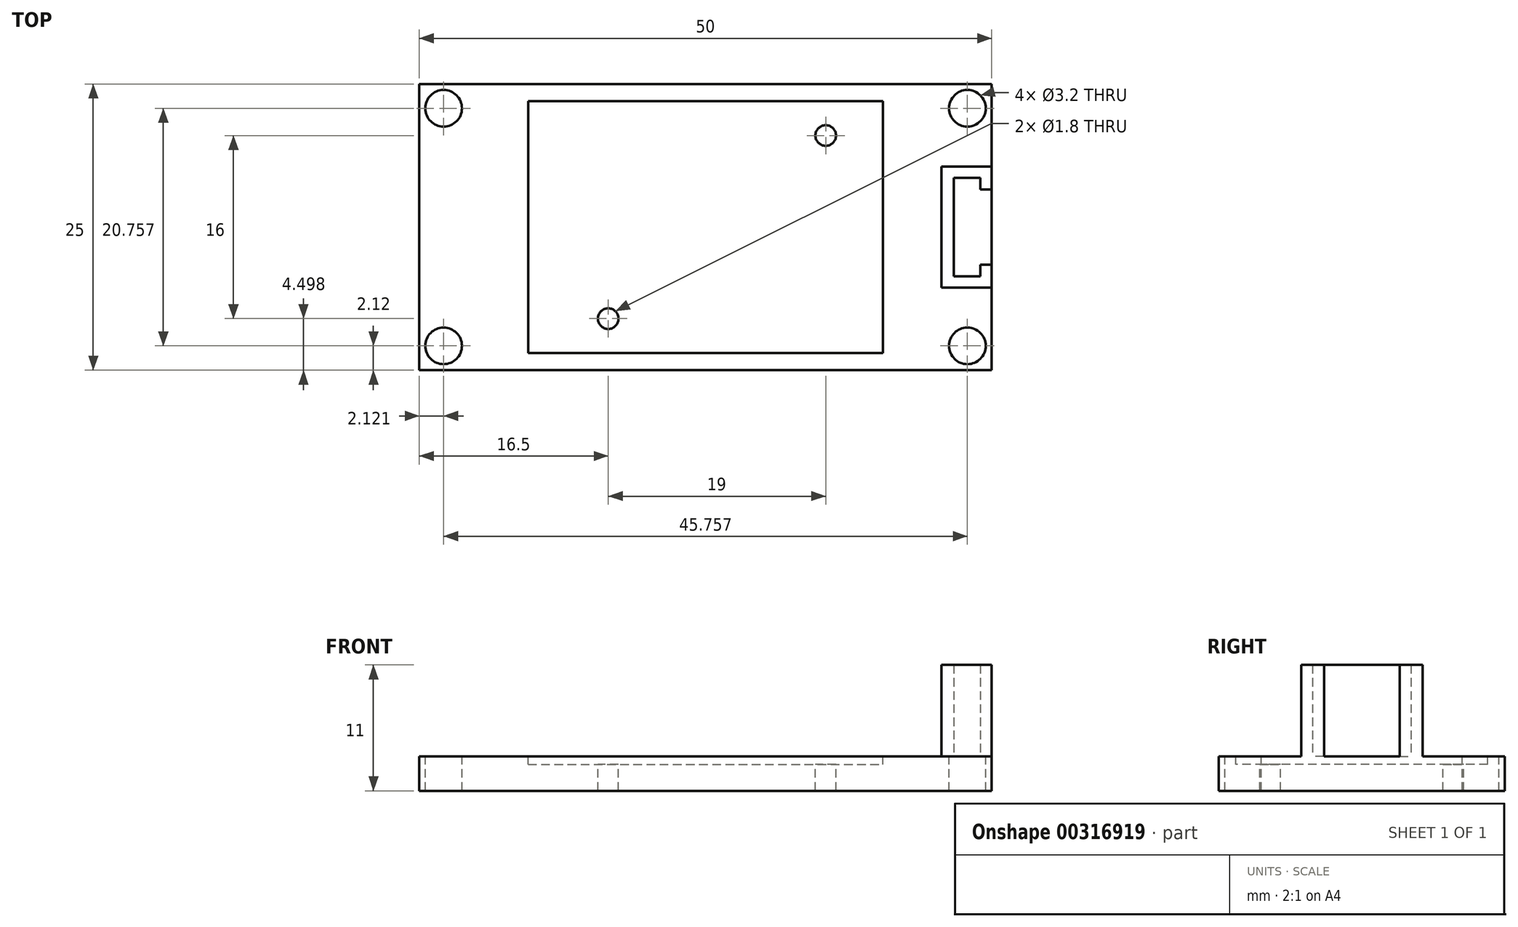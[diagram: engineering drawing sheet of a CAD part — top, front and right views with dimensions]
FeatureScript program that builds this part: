
annotation { "Feature Type Name" : "Feature", "Feature Type Description" : "" }
export const myFeature = defineFeature(function(context is Context, id is Id, definition is map)
    precondition{}
    {
        {
            var Q0;
            Q0=qCreatedBy(makeId("Top.planeOp"),FACE);
            var sketch = newSketch(context, id + "F0", { "sketchPlane" : qUnion([Q0])});
            skLineSegment(sketch, "E0.bottom", {"start": v(0, -1.45) * mm, "end": v(50, -1.45) * mm});
            skLineSegment(sketch, "E0.top", {"start": v(0, 23.55) * mm, "end": v(50, 23.55) * mm});
            skLineSegment(sketch, "E0.left", {"start": v(0, -1.45) * mm, "end": v(0, 23.55) * mm});
            skLineSegment(sketch, "E0.right", {"start": v(50, -1.45) * mm, "end": v(50, 23.55) * mm});
            skSolve(sketch);
        }
        {
            var Q0;
            Q0=makeQuery(id+"F0.imprint","IMPRINT",FACE,{"disambiguationData":[TD([[makeQuery(id+"F0.imprint","IMPRINT",EDGE,{"derivedFrom":sQuery(id+"F0.wireOp",EDGE,"E0.bottom")}),1.0]])]});
            extrude(context, id + "F1", {"entities" : qUnion([Q0]), "depth" : 3 * mm});
        }
        {
            var Q0;
            Q0=makeQuery(id+"F1.opExtrude","CAP_FACE",FACE,{"disambiguationData":[OSD([sQuery(id+"F0.wireOp",EDGE,"E0.bottom"),sQuery(id+"F0.wireOp",EDGE,"E0.top"),sQuery(id+"F0.wireOp",EDGE,"E0.left"),sQuery(id+"F0.wireOp",EDGE,"E0.right")])],"isStart":false});
            var sketch = newSketch(context, id + "F2", { "sketchPlane" : qUnion([Q0])});
            skLineSegment(sketch, "E1", {"start": v(0, 23.55) * mm, "end": v(2.12, 21.43) * mm});
            skLineSegment(sketch, "E2", {"start": v(50, 23.55) * mm, "end": v(47.88, 21.43) * mm});
            skLineSegment(sketch, "E3", {"start": v(50, -1.45) * mm, "end": v(47.88, 0.67) * mm});
            skLineSegment(sketch, "E4", {"start": v(0, -1.45) * mm, "end": v(2.12, 0.67) * mm});
            skSolve(sketch);
        }
        {
            var Q0;
            Q0=sQuery(id+"F2.wireOp",VERTEX,"E1.end");
            var Q1;
            Q1=sQuery(id+"F2.wireOp",VERTEX,"E2.end");
            var Q2;
            Q2=sQuery(id+"F2.wireOp",VERTEX,"E3.end");
            var Q3;
            Q3=sQuery(id+"F2.wireOp",VERTEX,"E4.end");
            var Q4;
            Q4=makeQuery(id+"F1.opExtrude","SWEPT_BODY",BODY,{"disambiguationData":[OSD([sQuery(id+"F0.wireOp",EDGE,"E0.bottom"),sQuery(id+"F0.wireOp",EDGE,"E0.top"),sQuery(id+"F0.wireOp",EDGE,"E0.left"),sQuery(id+"F0.wireOp",EDGE,"E0.right")])]});
            hole(context, id + "F3", {"style" : HoleStyle.SIMPLE, "endStyle" : HoleEndStyle.THROUGH, "holeDiameter" : 3.2 * mm, "isTappedThrough" : true, "tappedDepth" : 12 * mm, "tapClearance" : 3, "locations" : qUnion([Q0, Q1, Q2, Q3]), "scope" : qUnion([Q4])});
        }
        {
            var Q0;
            Q0=makeQuery(id+"F1.opExtrude","CAP_FACE",FACE,{"disambiguationData":[OSD([sQuery(id+"F0.wireOp",EDGE,"E0.bottom"),sQuery(id+"F0.wireOp",EDGE,"E0.top"),sQuery(id+"F0.wireOp",EDGE,"E0.left"),sQuery(id+"F0.wireOp",EDGE,"E0.right")])],"isStart":false});
            var sketch = newSketch(context, id + "F4", { "sketchPlane" : qUnion([Q0])});
            skLineSegment(sketch, "E5.bottom", {"start": v(9.5, 22.05) * mm, "end": v(40.5, 22.05) * mm});
            skLineSegment(sketch, "E5.top", {"start": v(9.5, 0.05) * mm, "end": v(40.5, 0.05) * mm});
            skLineSegment(sketch, "E5.left", {"start": v(9.5, 22.05) * mm, "end": v(9.5, 0.05) * mm});
            skLineSegment(sketch, "E5.right", {"start": v(40.5, 22.05) * mm, "end": v(40.5, 0.05) * mm});
            skSolve(sketch);
        }
        {
            var Q0;
            Q0=makeQuery(id+"F4.imprint","IMPRINT",FACE,{"disambiguationData":[TD([[makeQuery(id+"F4.imprint","IMPRINT",EDGE,{"derivedFrom":sQuery(id+"F4.wireOp",EDGE,"E5.bottom")}),-1.0]])]});
            extrude(context, id + "F5", {"entities" : qUnion([Q0]), "operationType" : NewBodyOperationType.REMOVE, "oppositeDirection" : true, "depth" : 0.7 * mm});
        }
        {
            var Q0;
            Q0=makeQuery(id+"F5.boolean.opBoolean","COPY",FACE,{"derivedFrom":makeQuery(id+"F5.opExtrude","CAP_FACE",FACE,{"disambiguationData":[OSD([sQuery(id+"F4.wireOp",EDGE,"E5.bottom"),sQuery(id+"F4.wireOp",EDGE,"E5.top"),sQuery(id+"F4.wireOp",EDGE,"E5.left"),sQuery(id+"F4.wireOp",EDGE,"E5.right")])],"isStart":false})});
            var sketch = newSketch(context, id + "F6", { "sketchPlane" : qUnion([Q0])});
            skLineSegment(sketch, "E6.bottom", {"start": v(10.5, 21.05) * mm, "end": v(39.5, 21.05) * mm});
            skLineSegment(sketch, "E6.top", {"start": v(10.5, 1.05) * mm, "end": v(39.5, 1.05) * mm});
            skLineSegment(sketch, "E6.left", {"start": v(10.5, 21.05) * mm, "end": v(10.5, 1.05) * mm});
            skLineSegment(sketch, "E6.right", {"start": v(39.5, 21.05) * mm, "end": v(39.5, 1.05) * mm});
            skPoint(sketch, "E7", {"position": v(10.5, 3.05) * mm});
            skPoint(sketch, "E8", {"position": v(16.5, 1.05) * mm});
            skPoint(sketch, "E9", {"position": v(35.5, 21.05) * mm});
            skPoint(sketch, "E10", {"position": v(39.5, 19.05) * mm});
            skLineSegment(sketch, "E11", {"start": v(35.5, 21.05) * mm, "end": v(35.5, 18.5) * mm});
            skLineSegment(sketch, "E12", {"start": v(39.5, 19.05) * mm, "end": v(34.03, 19.05) * mm});
            skLineSegment(sketch, "E13", {"start": v(10.5, 3.05) * mm, "end": v(17.92, 3.05) * mm});
            skLineSegment(sketch, "E14", {"start": v(16.5, 1.05) * mm, "end": v(16.5, 4.24) * mm});
            skPoint(sketch, "E15", {"position": v(35.5, 19.05) * mm});
            skPoint(sketch, "E16", {"position": v(16.5, 3.05) * mm});
            skSolve(sketch);
        }
        {
            var Q0;
            Q0=sQuery(id+"F6.wireOp",VERTEX,"E16");
            var Q1;
            Q1=sQuery(id+"F6.wireOp",VERTEX,"E15");
            var Q2;
            Q2=makeQuery(id+"F1.opExtrude","SWEPT_BODY",BODY,{"disambiguationData":[OSD([sQuery(id+"F0.wireOp",EDGE,"E0.bottom"),sQuery(id+"F0.wireOp",EDGE,"E0.top"),sQuery(id+"F0.wireOp",EDGE,"E0.left"),sQuery(id+"F0.wireOp",EDGE,"E0.right")])]});
            hole(context, id + "F7", {"style" : HoleStyle.SIMPLE, "endStyle" : HoleEndStyle.THROUGH, "holeDiameter" : 1.8 * mm, "tappedDepth" : 12 * mm, "tapClearance" : 3, "locations" : qUnion([Q0, Q1]), "scope" : qUnion([Q2])});
        }
        {
            var Q0;
            Q0=makeQuery(id+"F1.opExtrude","CAP_FACE",FACE,{"disambiguationData":[OSD([sQuery(id+"F0.wireOp",EDGE,"E0.bottom"),sQuery(id+"F0.wireOp",EDGE,"E0.top"),sQuery(id+"F0.wireOp",EDGE,"E0.left"),sQuery(id+"F0.wireOp",EDGE,"E0.right")])],"isStart":false});
            var sketch = newSketch(context, id + "F8", { "sketchPlane" : qUnion([Q0])});
            skPoint(sketch, "E17", {"position": v(50, 11.05) * mm});
            skPoint(sketch, "E18", {"position": v(49, 11.05) * mm});
            skLineSegment(sketch, "E19", {"start": v(49, 11.05) * mm, "end": v(49, 15.35) * mm});
            skLineSegment(sketch, "E20", {"start": v(49, 11.05) * mm, "end": v(49, 6.75) * mm});
            skLineSegment(sketch, "E21", {"start": v(49, 6.75) * mm, "end": v(46.7, 6.75) * mm});
            skLineSegment(sketch, "E22", {"start": v(49, 15.35) * mm, "end": v(46.7, 15.35) * mm});
            skLineSegment(sketch, "E23", {"start": v(46.7, 15.35) * mm, "end": v(46.7, 6.75) * mm});
            skLineSegment(sketch, "E24.top", {"start": v(49, 16.35) * mm, "end": v(45.6, 16.35) * mm});
            skLineSegment(sketch, "E24.right", {"start": v(45.6, 15.35) * mm, "end": v(45.6, 16.35) * mm});
            skLineSegment(sketch, "E25.left", {"start": v(45.6, 15.35) * mm, "end": v(45.6, 6.75) * mm});
            skLineSegment(sketch, "E26.top", {"start": v(45.6, 5.75) * mm, "end": v(49, 5.75) * mm});
            skLineSegment(sketch, "E26.left", {"start": v(45.6, 6.75) * mm, "end": v(45.6, 5.75) * mm});
            skLineSegment(sketch, "E27.bottom", {"start": v(49, 16.35) * mm, "end": v(50, 16.35) * mm});
            skLineSegment(sketch, "E27.top", {"start": v(49, 14.35) * mm, "end": v(50, 14.35) * mm});
            skLineSegment(sketch, "E27.right", {"start": v(50, 16.35) * mm, "end": v(50, 14.35) * mm});
            skLineSegment(sketch, "E28.bottom", {"start": v(49, 5.75) * mm, "end": v(50, 5.75) * mm});
            skLineSegment(sketch, "E28.top", {"start": v(49, 7.75) * mm, "end": v(50, 7.75) * mm});
            skLineSegment(sketch, "E28.right", {"start": v(50, 5.75) * mm, "end": v(50, 7.75) * mm});
            skSolve(sketch);
        }
        {
            var Q0;
            {var subQ3=sQuery(id+"F8.wireOp",EDGE,"E21");Q0=makeQuery(id+"F8.imprint","IMPRINT",FACE,{"disambiguationData":[TD([[makeQuery(id+"F8.imprint","IMPRINT",EDGE,{"derivedFrom":subQ3}),1.0]])]});}
            extrude(context, id + "F9", {"entities" : qUnion([Q0]), "operationType" : NewBodyOperationType.ADD, "depth" : 8 * mm});
        }
    });
